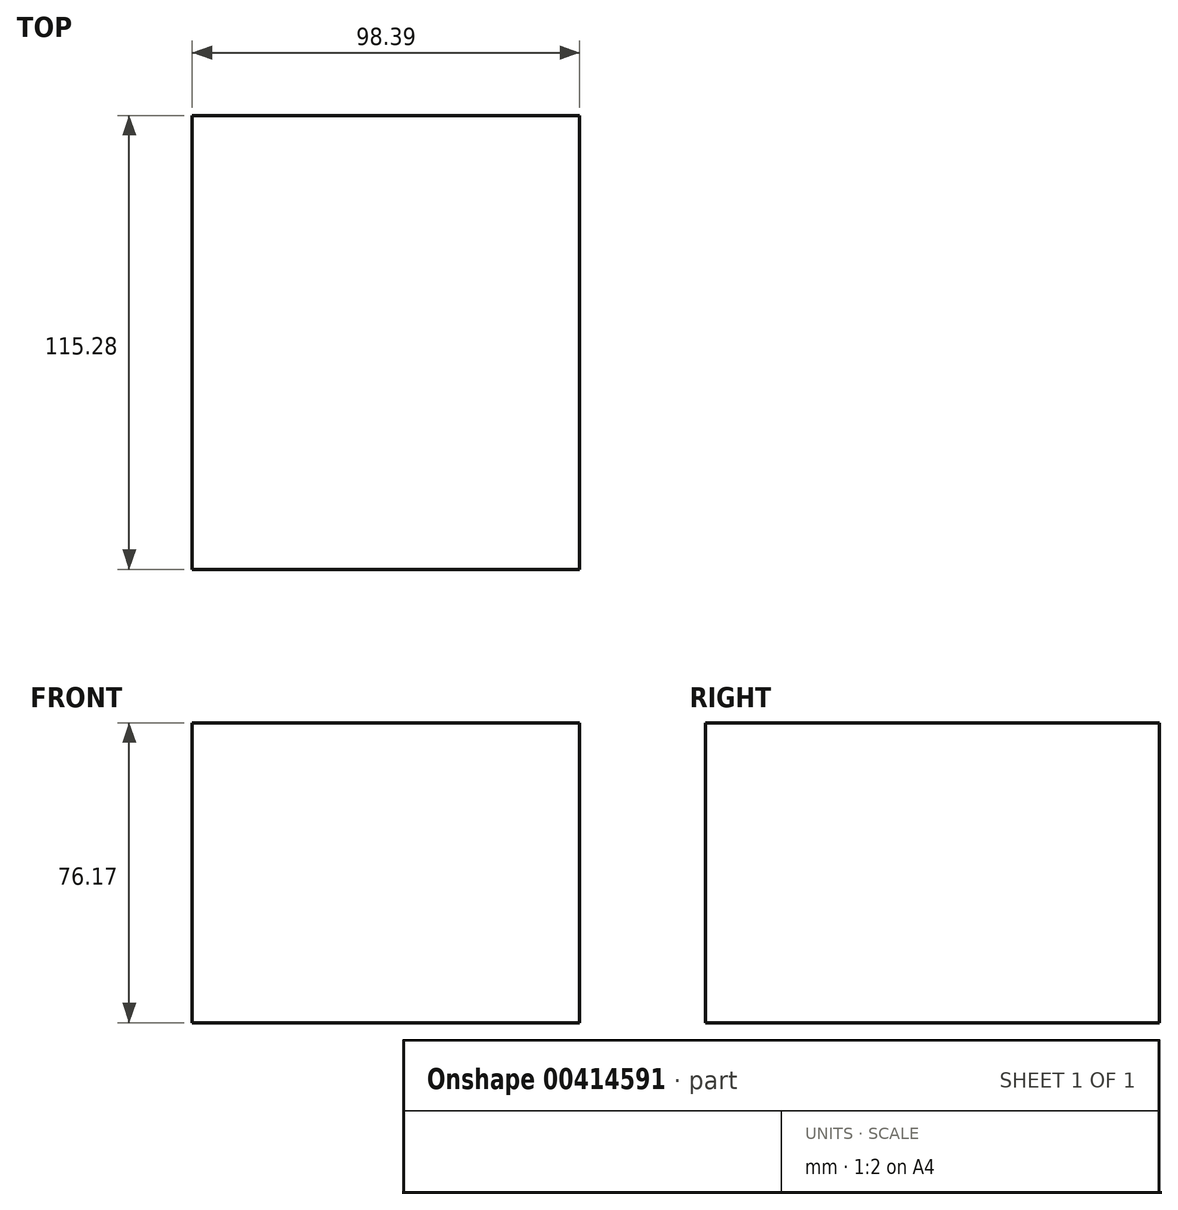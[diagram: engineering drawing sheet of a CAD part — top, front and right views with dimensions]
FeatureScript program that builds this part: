
annotation { "Feature Type Name" : "Feature", "Feature Type Description" : "" }
export const myFeature = defineFeature(function(context is Context, id is Id, definition is map)
    precondition{}
    {
        {
            var Q0;
            Q0=qCreatedBy(makeId("Front.planeOp"),FACE);
            var sketch = newSketch(context, id + "F0", { "sketchPlane" : qUnion([Q0])});
            skLineSegment(sketch, "E0.bottom", {"start": v(8.7, 12.49) * mm, "end": v(-89.7, 12.49) * mm});
            skLineSegment(sketch, "E0.top", {"start": v(8.7, 88.66) * mm, "end": v(-89.7, 88.66) * mm});
            skLineSegment(sketch, "E0.left", {"start": v(8.7, 12.49) * mm, "end": v(8.7, 88.66) * mm});
            skLineSegment(sketch, "E0.right", {"start": v(-89.7, 12.49) * mm, "end": v(-89.7, 88.66) * mm});
            skSolve(sketch);
        }
        {
            var Q0;
            Q0 = qSketchRegion(id + "F0", true);
            extrude(context, id + "F1", {"entities" : qUnion([Q0]), "depth" : 89.88 * mm});
        }
        {
            var Q0;
            Q0=makeQuery(id+"F1.opExtrude","CAP_FACE",FACE,{"disambiguationData":[OSD([sQuery(id+"F0.wireOp",EDGE,"E0.bottom"),sQuery(id+"F0.wireOp",EDGE,"E0.top"),sQuery(id+"F0.wireOp",EDGE,"E0.left"),sQuery(id+"F0.wireOp",EDGE,"E0.right")])],"isStart":true});
            extrude(context, id + "F2", {"entities" : qUnion([Q0]), "operationType" : NewBodyOperationType.ADD, "depth" : 25.4 * mm});
        }
    });
